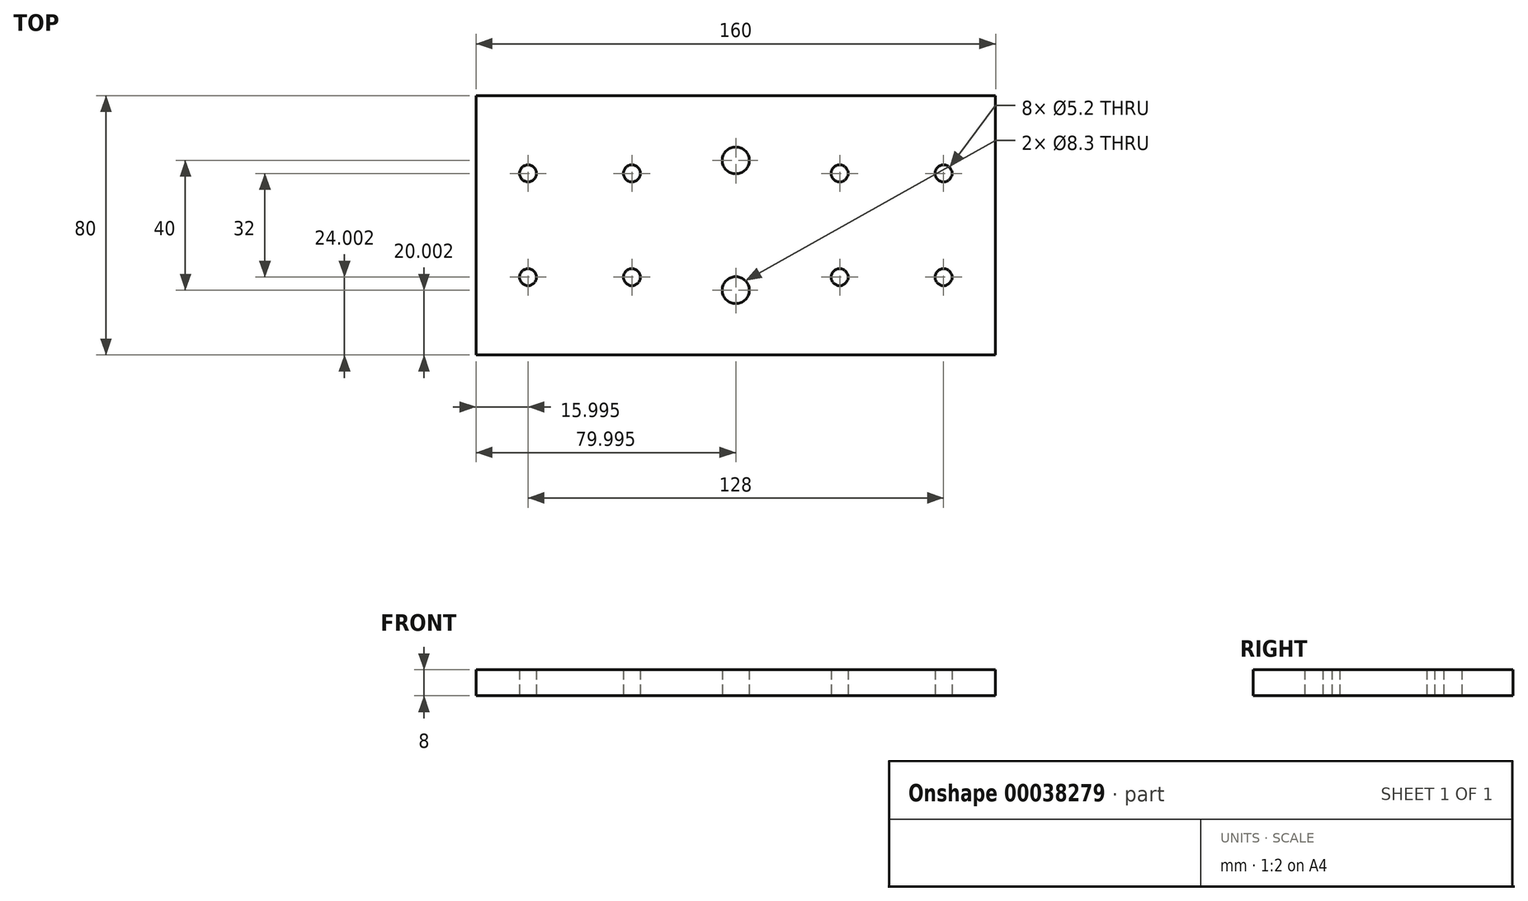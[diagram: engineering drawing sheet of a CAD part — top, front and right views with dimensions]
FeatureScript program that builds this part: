
annotation { "Feature Type Name" : "Feature", "Feature Type Description" : "" }
export const myFeature = defineFeature(function(context is Context, id is Id, definition is map)
    precondition{}
    {
        {
            var Q0;
            Q0=qCreatedBy(makeId("Top.planeOp"),FACE);
            var sketch = newSketch(context, id + "F0", { "sketchPlane" : qUnion([Q0])});
            skLineSegment(sketch, "E0.bottom", {"start": v(-68.17, 42.31) * mm, "end": v(91.83, 42.31) * mm});
            skLineSegment(sketch, "E0.top", {"start": v(-68.17, -37.69) * mm, "end": v(91.83, -37.69) * mm});
            skLineSegment(sketch, "E0.left", {"start": v(-68.17, 42.31) * mm, "end": v(-68.17, -37.69) * mm});
            skLineSegment(sketch, "E0.right", {"start": v(91.83, 42.31) * mm, "end": v(91.83, -37.69) * mm});
            skPoint(sketch, "E1", {"position": v(-20.17, 18.31) * mm});
            skPoint(sketch, "E2", {"position": v(43.83, 18.31) * mm});
            skPoint(sketch, "E3", {"position": v(-20.17, -13.69) * mm});
            skPoint(sketch, "E4", {"position": v(43.83, -13.69) * mm});
            skPoint(sketch, "E5", {"position": v(75.83, 18.31) * mm});
            skPoint(sketch, "E6", {"position": v(75.83, -13.69) * mm});
            skPoint(sketch, "E7", {"position": v(-52.17, -13.69) * mm});
            skPoint(sketch, "E8", {"position": v(-52.17, 18.31) * mm});
            skPoint(sketch, "E9", {"position": v(11.83, 22.31) * mm});
            skPoint(sketch, "E10", {"position": v(11.83, -17.69) * mm});
            skCircle(sketch, "E11", {"center": v(-52.17, 18.31) * mm, "radius": 2.6 * mm});
            skCircle(sketch, "E12.0.1.0", {"center": v(-52.17, -13.69) * mm, "radius": 2.6 * mm});
            skCircle(sketch, "E12.1.0.0", {"center": v(-20.17, 18.31) * mm, "radius": 2.6 * mm});
            skCircle(sketch, "E12.1.1.0", {"center": v(-20.17, -13.69) * mm, "radius": 2.6 * mm});
            skLineSegment(sketch, "E12.direction1", {"start": v(-52.17, 18.31) * mm, "end": v(-20.17, 18.31) * mm, "construction": true});
            skLineSegment(sketch, "E12.direction2", {"start": v(-52.17, 18.31) * mm, "end": v(-52.17, -13.69) * mm, "construction": true});
            skCircle(sketch, "E13", {"center": v(43.83, 18.31) * mm, "radius": 2.6 * mm});
            skCircle(sketch, "E14.0.1.0", {"center": v(43.83, -13.69) * mm, "radius": 2.6 * mm});
            skCircle(sketch, "E14.1.0.0", {"center": v(75.83, 18.31) * mm, "radius": 2.6 * mm});
            skCircle(sketch, "E14.1.1.0", {"center": v(75.83, -13.69) * mm, "radius": 2.6 * mm});
            skLineSegment(sketch, "E14.direction1", {"start": v(43.83, 18.31) * mm, "end": v(75.83, 18.31) * mm, "construction": true});
            skLineSegment(sketch, "E14.direction2", {"start": v(43.83, 18.31) * mm, "end": v(43.83, -13.69) * mm, "construction": true});
            skCircle(sketch, "E15", {"center": v(11.83, 22.31) * mm, "radius": 4.15 * mm});
            skCircle(sketch, "E16", {"center": v(11.83, -17.69) * mm, "radius": 4.15 * mm});
            skSolve(sketch);
        }
        {
            var Q0;
            Q0 = qSketchRegion(id + "F0", true);
            extrude(context, id + "F1", {"entities" : qUnion([Q0]), "depth" : 8 * mm});
        }
    });
